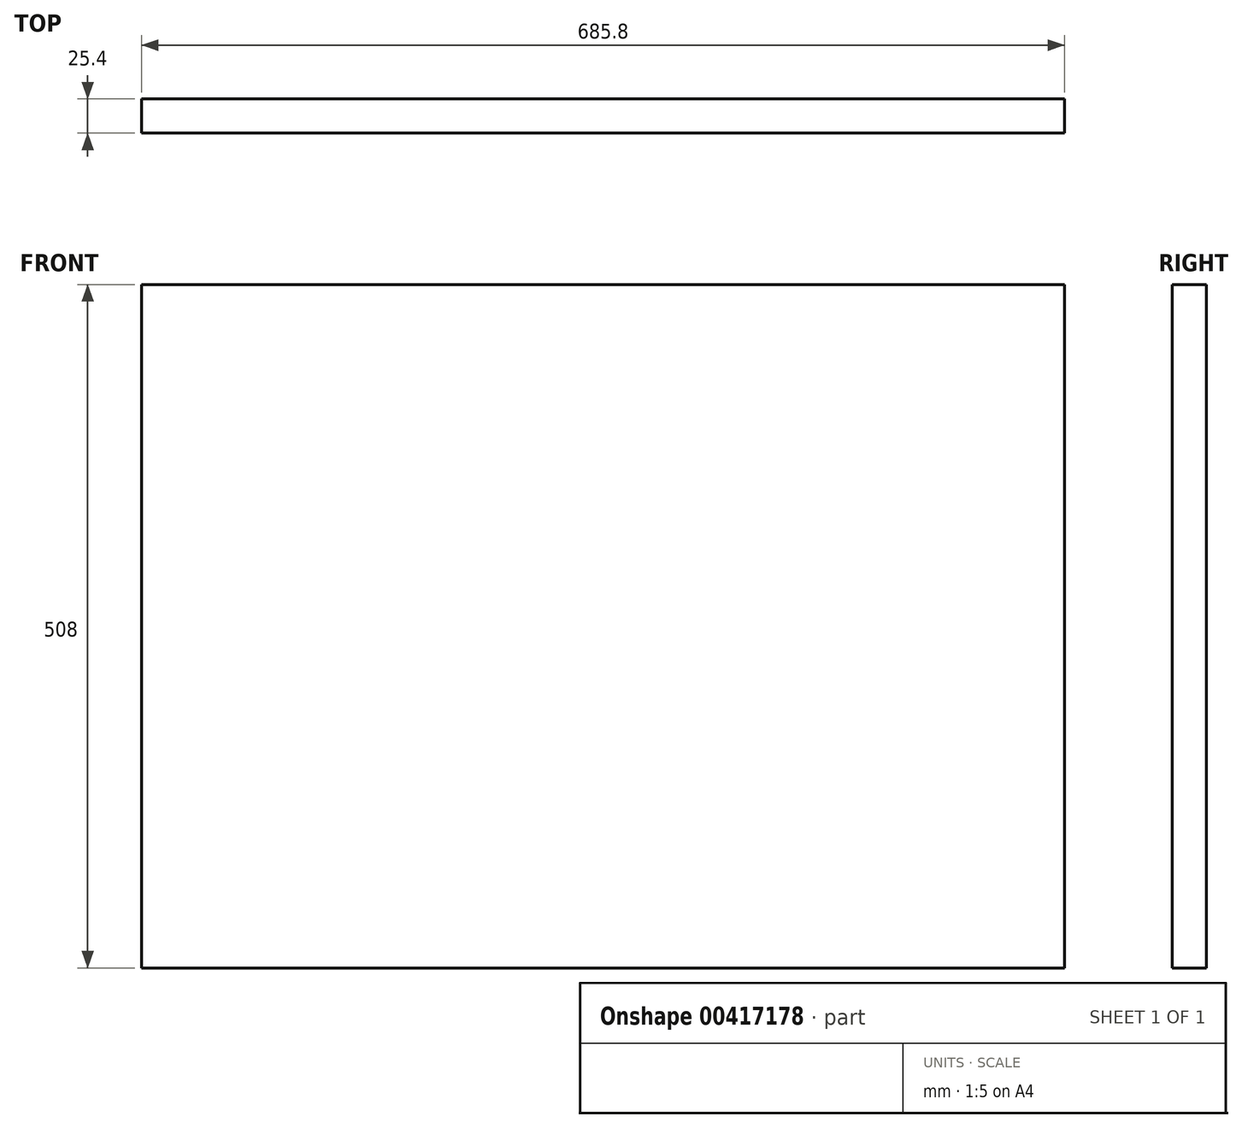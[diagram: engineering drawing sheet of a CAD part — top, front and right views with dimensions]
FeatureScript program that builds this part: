
annotation { "Feature Type Name" : "Feature", "Feature Type Description" : "" }
export const myFeature = defineFeature(function(context is Context, id is Id, definition is map)
    precondition{}
    {
        {
            var Q0;
            Q0=qCreatedBy(makeId("Front.planeOp"),FACE);
            var sketch = newSketch(context, id + "F0", { "sketchPlane" : qUnion([Q0])});
            skLineSegment(sketch, "E0.bottom", {"start": v(0, 0) * mm, "end": v(685.8, 0) * mm});
            skLineSegment(sketch, "E0.top", {"start": v(0, 508) * mm, "end": v(685.8, 508) * mm});
            skLineSegment(sketch, "E0.left", {"start": v(0, 0) * mm, "end": v(0, 508) * mm});
            skLineSegment(sketch, "E0.right", {"start": v(685.8, 0) * mm, "end": v(685.8, 508) * mm});
            skSolve(sketch);
        }
        {
            var Q0;
            Q0=makeQuery(id+"F0.imprint","IMPRINT",FACE,{"disambiguationData":[TD([[makeQuery(id+"F0.imprint","IMPRINT",EDGE,{"derivedFrom":sQuery(id+"F0.wireOp",EDGE,"E0.bottom")}),1.0]])]});
            extrude(context, id + "F1", {"entities" : qUnion([Q0]), "oppositeDirection" : true, "depth" : 25.4 * mm});
        }
    });
